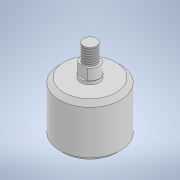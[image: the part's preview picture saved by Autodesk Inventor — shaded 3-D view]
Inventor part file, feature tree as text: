
AUTODESK INVENTOR PART (.ipt)
format: ipt  version: 2022 (Build 260153000, 153)  size: 156,672 bytes
history: native  units: in
note: dims shown in document units (in); Inventor stores cm internally (conversion verified against a paired STEP export)
features: sketch x3, extrude x2, revolve x1, chamfer x1, thread x1, projected_geometry x1
ambient origin geometry x8: Origin, YZ Plane, XZ Plane, XY Plane, X Axis, Y Axis, Z Axis, Center Point
bodies: Solid1 (feature_tree)
feature tree (9):
  revolve  "Revolution1"  [1 undecoded]
  chamfer  "Chamfer1"  Distance=0.2362in
  thread  "Thread1"  [1 undecoded]
  extrude  "Extrusion1"  Depth=1.4961in
  extrude  "Extrusion3"  TaperAngle=90.0deg  [1 undecoded]
  sketch  "Sketch1"  dims[d0=1.1024in d1=0.9449in]
  sketch  "Sketch2"  dims[d2=0.1969in]
  projected_geometry  "Projected Loop1"
  sketch  "Sketch4"  dims[d3=0.315in d4=0.2362in d5=0.3346in d6=1.4961in d7=90.0deg d8=0.0787in d9=0.0787in d10=45.0deg d11=0.2976in d12=0.0in d13=0.265in d14=0.1969in d15=0.0in d20=0.1181in d21=0.748in d22=0.6299in d23=45.0deg d24=0.1969in d25=0.0in]
note: 3 required parameter values undecoded (feature->parameter linkage not recoverable at this tier; creation-order binding heuristic only, values carry confidence <= 0.55)